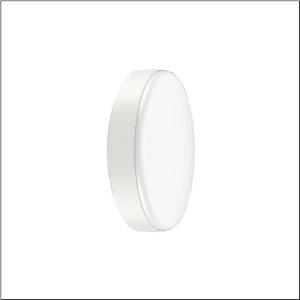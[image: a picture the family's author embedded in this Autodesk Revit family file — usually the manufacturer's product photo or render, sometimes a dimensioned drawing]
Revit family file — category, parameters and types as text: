
# Revit family: rondel_31_51wc10db44a
name_source: partatom
category: Lighting Fixtures
units: mm (PartAtom-declared; Revit-internal decimal feet)

## family parameters
Cut with Voids When Loaded = No
Host = Face
Light Source = No
Part Type = Normal
Room Calculation Point = No
Round Connector Dimension = Use Diameter
Shared = No

## types (1)
- Rondel 31 (1 x LED, 4400 lm, 34 W, 4000K)
    Apparent Load = 34 VA
    CIE Flux Codes = 44 75 94 94 100
    Color Rendering = 80
    Color Temperature = 4000K
    Default Elevation = 1800 mm
    Description = Rondel 31, wall and ceiling luminaire, primary optical cover: cover, of PC, opal, light emission: direct distribution, primary light characteristic: symmetric, installation type: surface-mounted, LED, rated luminous flux: 4.400lm, luminous efficacy: 129lm/W, light colour: 840, colour temperature: 4000K, with terminal, 3-pole, max. 2.5mm², mains connection: 220..240V, AC, 50/60Hz, rated input power: 34W, luminaire housing, of PC, traffic white (RAL 9016), diameter: 480mm, protection rating (complete): IP65, insulation class (complete): insulation class II (safety insulation), certification: CE, impact resistance: IK10, permissible operating ambient temperature: -20..+40°C, permissible storage temperature: -20..+60°C, packaging unit: 1 piece
    Height = 97 mm
    Lamp = 1 x LED
    Lamp Light Flux = 4400 lm
    Lamp Power = 34 W
    Lamp count = 1
    Length = 480 mm
    Luminous efficacy = 129 lm/W
    Manufacturer = Siteco
    ModVariant = No
    Model = 51WC10DB44A
    Mounting Place = Ceiling
    Mounting Type = Surface mounted
    Number of Poles = 1
    OnlyDefault = Yes
    Power Factor = 1
    Product Name = Rondel 31
    Product group = wall and ceiling luminaire
    ProductGroupID = 301
    Protection Class = Protection class II
    Protection Degree = IP 65
    RLX_Detail_Level = 1
    RLX_Emergency_Light_Flux = 0 lm
    RLX_Emergency_Type = 0
    RLX_Emergency_Type_DB = No
    RlxData = <blob elided: 40849 chars, md5=6bd57316>
    Socket = socket
    Standby Power = 0 W
    System Light Flux = 4400 lm
    System Power = 34 W
    Type Comments = Product without accessories
    Type Image = l_1007188.jpg
    URL = http://relux.com
    VarID = ---
    Voltage = 0 V
    Weight = 0.00 kg
    Width = 0 mm  [stored 0 ft]

note: [stored X ft] marks values corroborated as IEEE doubles in the binary element streams (Revit-internal decimal feet)

## geometry (parser evidence)
native form markers: Blend x4, Sweep x13
no freeform markers — native parametric forms only
